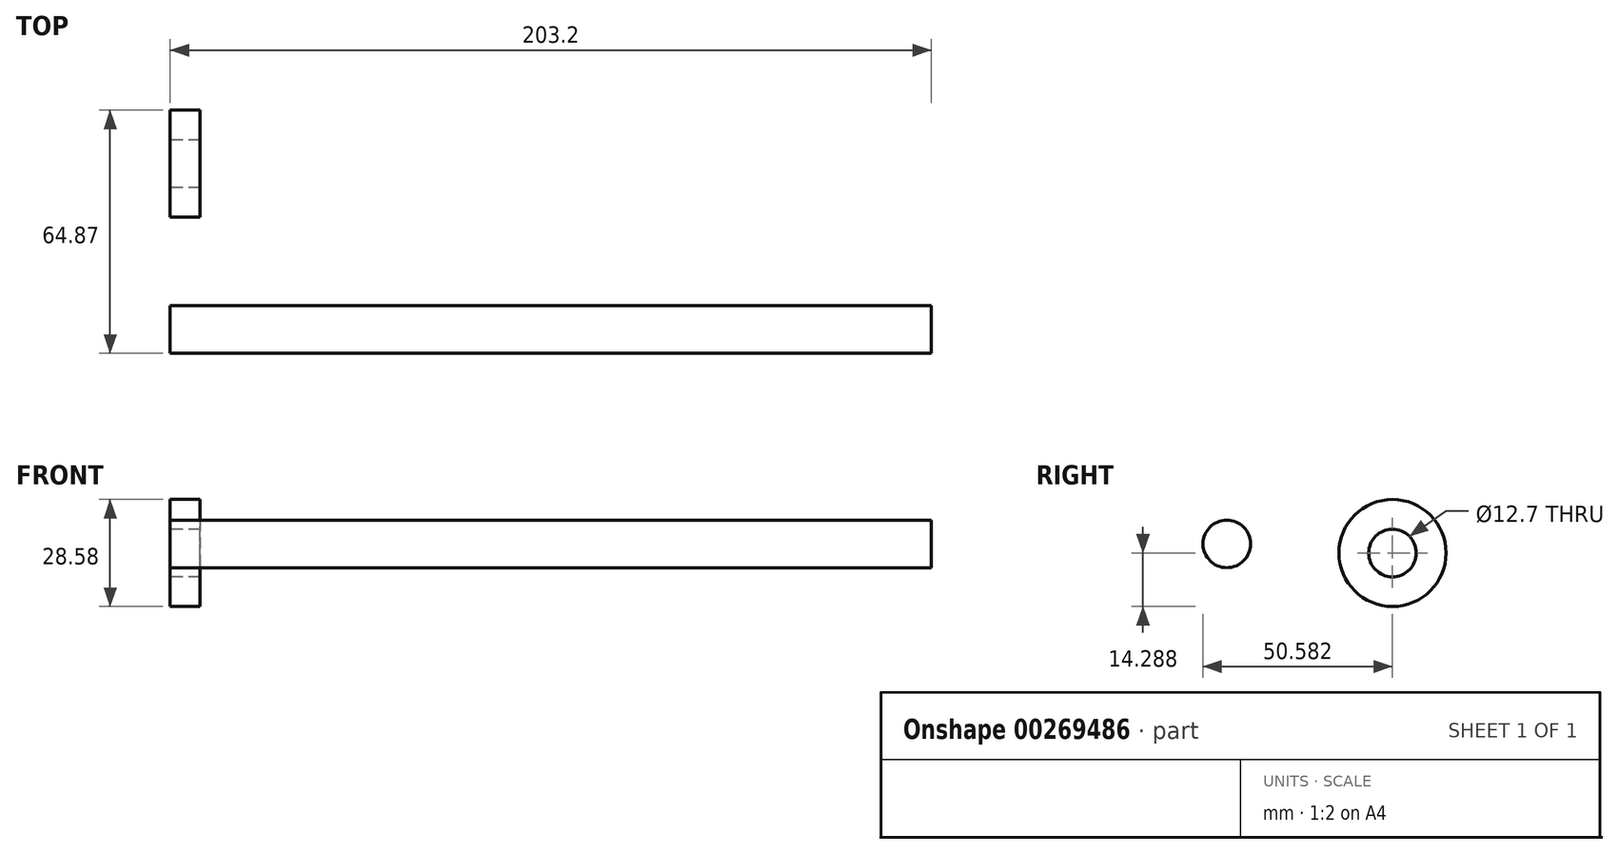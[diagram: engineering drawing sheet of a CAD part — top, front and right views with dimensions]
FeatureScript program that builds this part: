
annotation { "Feature Type Name" : "Feature", "Feature Type Description" : "" }
export const myFeature = defineFeature(function(context is Context, id is Id, definition is map)
    precondition{}
    {
        {
            var Q0;
            Q0=qCreatedBy(makeId("Right.planeOp"),FACE);
            var sketch = newSketch(context, id + "F0", { "sketchPlane" : qUnion([Q0])});
            skCircle(sketch, "E0", {"center": v(-15.34, 32.9) * mm, "radius": 6.35 * mm});
            skSolve(sketch);
        }
        {
            var Q0;
            Q0=makeQuery(id+"F0.imprint","IMPRINT",FACE,{"disambiguationData":[TD([[makeQuery(id+"F0.imprint","IMPRINT",EDGE,{"derivedFrom":sQuery(id+"F0.wireOp",EDGE,"E0")}),1.0]])]});
            extrude(context, id + "F1", {"entities" : qUnion([Q0]), "depth" : 203.2 * mm, "offsetDistance" : 25.4 * mm});
        }
        {
            var Q0;
            Q0=qCreatedBy(makeId("Right.planeOp"),FACE);
            var sketch = newSketch(context, id + "F2", { "sketchPlane" : qUnion([Q0])});
            skCircle(sketch, "E1", {"center": v(28.9, 30.45) * mm, "radius": 6.35 * mm});
            skCircle(sketch, "E2", {"center": v(28.9, 30.45) * mm, "radius": 14.29 * mm});
            skSolve(sketch);
        }
        {
            var Q0;
            Q0=makeQuery(id+"F2.imprint","IMPRINT",FACE,{"disambiguationData":[TD([[makeQuery(id+"F2.imprint","IMPRINT",EDGE,{"derivedFrom":sQuery(id+"F2.wireOp",EDGE,"E1")}),-1.0]])]});
            extrude(context, id + "F3", {"entities" : qUnion([Q0]), "depth" : 7.92 * mm});
        }
    });
